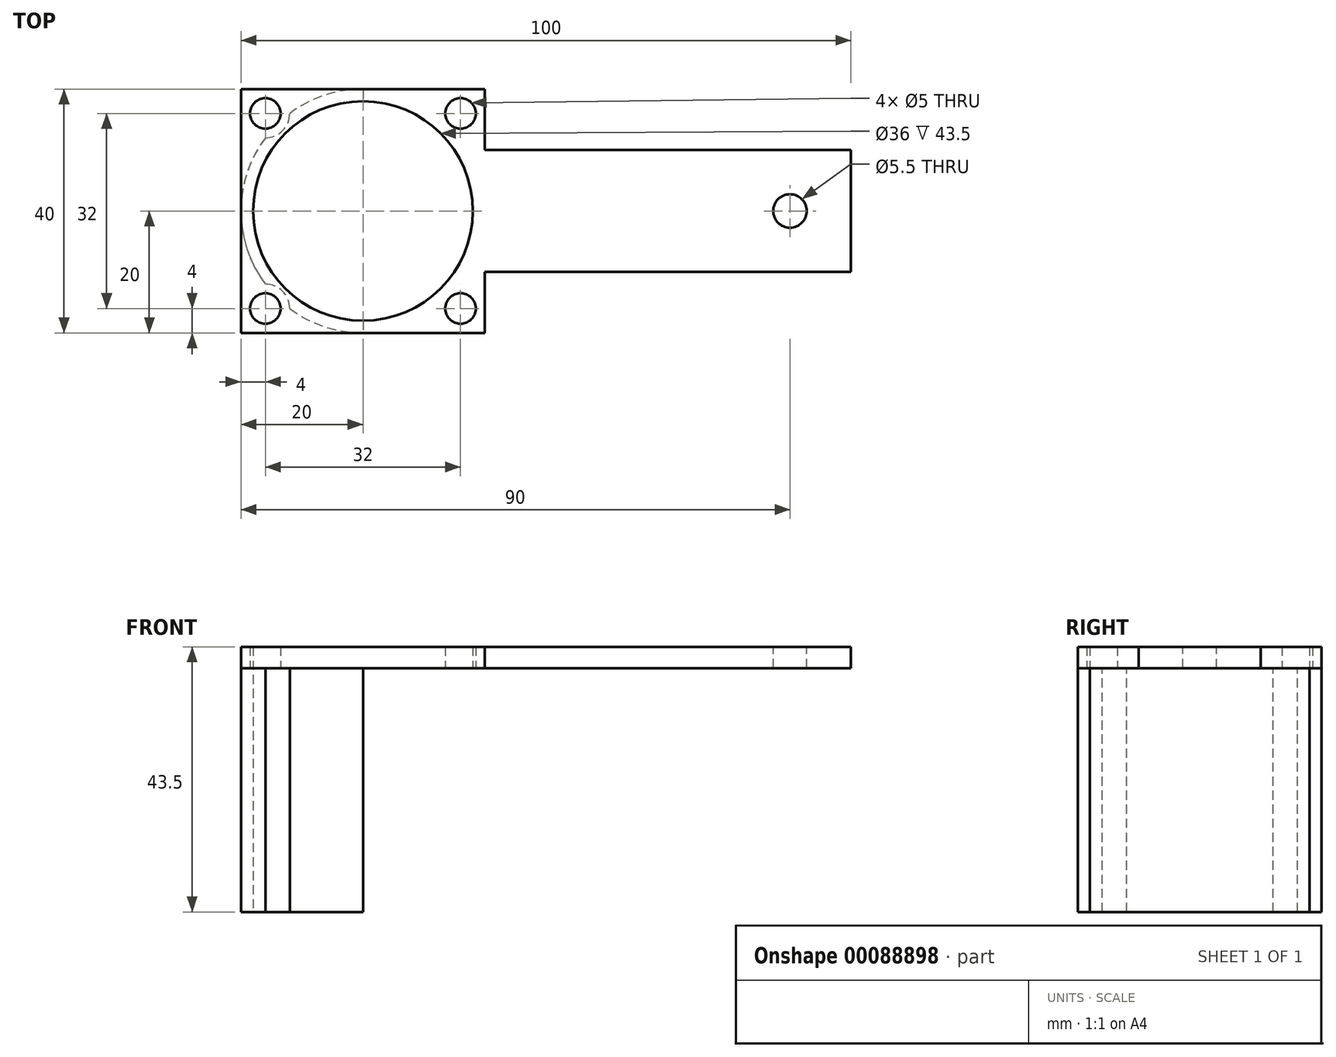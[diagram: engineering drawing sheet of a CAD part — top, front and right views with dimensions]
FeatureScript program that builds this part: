
annotation { "Feature Type Name" : "Feature", "Feature Type Description" : "" }
export const myFeature = defineFeature(function(context is Context, id is Id, definition is map)
    precondition{}
    {
        {
            var Q0;
            Q0=qCreatedBy(makeId("Top.planeOp"),FACE);
            var sketch = newSketch(context, id + "F0", { "sketchPlane" : qUnion([Q0])});
            skLineSegment(sketch, "E0.bottom", {"start": v(0, 0) * mm, "end": v(40, 0) * mm});
            skLineSegment(sketch, "E0.top", {"start": v(0, 40) * mm, "end": v(40, 40) * mm});
            skLineSegment(sketch, "E0.left", {"start": v(0, 0) * mm, "end": v(0, 40) * mm});
            skLineSegment(sketch, "E1", {"start": v(-47.65, 20) * mm, "end": v(85.15, 20) * mm, "construction": true});
            skCircle(sketch, "E2", {"center": v(20, 20) * mm, "radius": 18 * mm});
            skLineSegment(sketch, "E3", {"start": v(20, 54.43) * mm, "end": v(20, -19.34) * mm, "construction": true});
            skCircle(sketch, "E4", {"center": v(4, 36) * mm, "radius": 2.5 * mm});
            skCircle(sketch, "E5.1.0", {"center": v(4, 4) * mm, "radius": 2.5 * mm});
            skCircle(sketch, "E5.2.0", {"center": v(36, 4) * mm, "radius": 2.5 * mm});
            skCircle(sketch, "E5.3.0", {"center": v(36, 36) * mm, "radius": 2.5 * mm});
            skLineSegment(sketch, "E6", {"start": v(20, 20) * mm, "end": v(0, 40) * mm, "construction": true});
            skLineSegment(sketch, "E7", {"start": v(40, 40) * mm, "end": v(40, 0) * mm});
            skSolve(sketch);
        }
        {
            var Q0;
            Q0=makeQuery(id+"F0.imprint","IMPRINT",FACE,{"disambiguationData":[TD([[makeQuery(id+"F0.imprint","IMPRINT",EDGE,{"derivedFrom":sQuery(id+"F0.wireOp",EDGE,"E0.bottom")}),1.0]])]});
            extrude(context, id + "F1", {"entities" : qUnion([Q0]), "depth" : 3.5 * mm});
        }
        {
            var Q0;
            Q0=makeQuery(id+"F1.opExtrude","CAP_FACE",FACE,{"disambiguationData":[OSD([sQuery(id+"F0.wireOp",EDGE,"E0.bottom"),sQuery(id+"F0.wireOp",EDGE,"E0.top"),sQuery(id+"F0.wireOp",EDGE,"E0.left"),sQuery(id+"F0.wireOp",EDGE,"E2"),sQuery(id+"F0.wireOp",EDGE,"E4"),sQuery(id+"F0.wireOp",EDGE,"E5.1.0"),sQuery(id+"F0.wireOp",EDGE,"E5.2.0"),sQuery(id+"F0.wireOp",EDGE,"E5.3.0"),sQuery(id+"F0.wireOp",EDGE,"E7")])],"isStart":false});
            var sketch = newSketch(context, id + "F2", { "sketchPlane" : qUnion([Q0])});
            skLineSegment(sketch, "E8.bottom", {"start": v(40, 10) * mm, "end": v(100, 10) * mm});
            skLineSegment(sketch, "E8.top", {"start": v(40, 30) * mm, "end": v(100, 30) * mm});
            skLineSegment(sketch, "E8.left", {"start": v(40, 10) * mm, "end": v(40, 30) * mm});
            skLineSegment(sketch, "E8.right", {"start": v(100, 10) * mm, "end": v(100, 30) * mm});
            skCircle(sketch, "E9", {"center": v(90, 20) * mm, "radius": 2.75 * mm});
            skSolve(sketch);
        }
        {
            var Q0;
            Q0=qSketchRegion(id+"F2",true);
            var Q1;
            Q1=makeQuery(id+"F1.opExtrude","CAP_FACE",FACE,{"disambiguationData":[OSD([sQuery(id+"F0.wireOp",EDGE,"E0.bottom"),sQuery(id+"F0.wireOp",EDGE,"E0.top"),sQuery(id+"F0.wireOp",EDGE,"E0.left"),sQuery(id+"F0.wireOp",EDGE,"E2"),sQuery(id+"F0.wireOp",EDGE,"E4"),sQuery(id+"F0.wireOp",EDGE,"E5.1.0"),sQuery(id+"F0.wireOp",EDGE,"E5.2.0"),sQuery(id+"F0.wireOp",EDGE,"E5.3.0"),sQuery(id+"F0.wireOp",EDGE,"E7")])],"isStart":true});
            extrude(context, id + "F3", {"entities" : qUnion([Q0]), "operationType" : NewBodyOperationType.ADD, "endBound" : BoundingType.UP_TO_SURFACE, "oppositeDirection" : true, "endBoundEntityFace" : qUnion([Q1]), "depth" : 25 * mm});
        }
        {
            var Q0;
            Q0=qCreatedBy(makeId("Top.planeOp"),FACE);
            cPlane(context, id + "F4", {"entities" : qUnion([Q0]), "cplaneType" : CPlaneType.OFFSET, "offset" : 40 * mm, "oppositeDirection" : true, "width" : 150 * mm, "height" : 150 * mm});
        }
        {
            var Q0;
            Q0=qCreatedBy(makeId("Top.planeOp"),FACE);
            var sketch = newSketch(context, id + "F5", { "sketchPlane" : qUnion([Q0])});
            skArc(sketch, "E10", {"start": v(10, 2.68) * mm, "mid": v(20, 0) * mm, "end": v(30, 2.68) * mm});
            skArc(sketch, "E11", {"start": v(30, 2.68) * mm, "mid": v(40, 20) * mm, "end": v(30, 37.32) * mm});
            skArc(sketch, "E12", {"start": v(10, 37.32) * mm, "mid": v(0, 20) * mm, "end": v(10, 2.68) * mm});
            skArc(sketch, "E13", {"start": v(30, 37.32) * mm, "mid": v(20, 40) * mm, "end": v(10, 37.32) * mm});
            skLineSegment(sketch, "E14", {"start": v(10, -19.1) * mm, "end": v(10, 62.07) * mm, "construction": true});
            skLineSegment(sketch, "E15.MirrorCS", {"start": v(30, -19.1) * mm, "end": v(30, 62.07) * mm, "construction": true});
            skSolve(sketch);
        }
        {
            var Q0;
            Q0=makeQuery(id+"F0.imprint","IMPRINT",FACE,{"disambiguationData":[TD([[makeQuery(id+"F0.imprint","IMPRINT",EDGE,{"derivedFrom":sQuery(id+"F0.wireOp",EDGE,"E0.bottom")}),1.0]])]});
            var sketch = newSketch(context, id + "F6", { "sketchPlane" : qUnion([Q0])});
            skArc(sketch, "E16", {"start": v(20, 40) * mm, "mid": v(0, 20) * mm, "end": v(20, 0) * mm});
            skArc(sketch, "E17", {"start": v(20, 38) * mm, "mid": v(2, 20) * mm, "end": v(20, 2) * mm});
            skLineSegment(sketch, "E18", {"start": v(20, 40) * mm, "end": v(20, 38) * mm});
            skLineSegment(sketch, "E19.trimOffspring", {"start": v(20, 2) * mm, "end": v(20, 0) * mm});
            skSolve(sketch);
        }
        {
            var Q0;
            Q0 = qSketchRegion(id + "F6", true);
            var Q1;
            Q1=qCreatedBy(id+"F4.planeOp",FACE);
            extrude(context, id + "F7", {"entities" : qUnion([Q0]), "operationType" : NewBodyOperationType.ADD, "endBound" : BoundingType.UP_TO_SURFACE, "oppositeDirection" : true, "endBoundEntityFace" : qUnion([Q1]), "depth" : 25 * mm});
        }
        {
            var Q0;
            Q0=makeQuery(id+"F0.imprint","IMPRINT",FACE,{"disambiguationData":[TD([[makeQuery(id+"F0.imprint","IMPRINT",EDGE,{"derivedFrom":sQuery(id+"F0.wireOp",EDGE,"E0.bottom")}),1.0]])]});
            var sketch = newSketch(context, id + "F8", { "sketchPlane" : qUnion([Q0])});
            skCircle(sketch, "E20", {"center": v(36, 36) * mm, "radius": 4 * mm});
            skCircle(sketch, "E21.MirrorC", {"center": v(4, 36) * mm, "radius": 4 * mm});
            skCircle(sketch, "E22.MirrorC", {"center": v(4, 4) * mm, "radius": 4 * mm});
            skCircle(sketch, "E23.MirrorC", {"center": v(36, 4) * mm, "radius": 4 * mm});
            skSolve(sketch);
        }
        {
            var Q0;
            Q0=qSketchRegion(id+"F8",true);
            var Q1;
            Q1=makeQuery(id+"FzZSrTWy1jUC6FN_1.opExtrude","CAP_FACE",FACE,{"disambiguationData":[OSD([dummyQuery(id+"F4.planeOp",FACE)])],"isStart":false});
            extrude(context, id + "F9", {"entities" : qUnion([Q0]), "operationType" : NewBodyOperationType.REMOVE, "endBound" : BoundingType.THROUGH_ALL, "oppositeDirection" : true, "endBoundEntityFace" : qUnion([Q1]), "depth" : 25 * mm});
        }
    });
